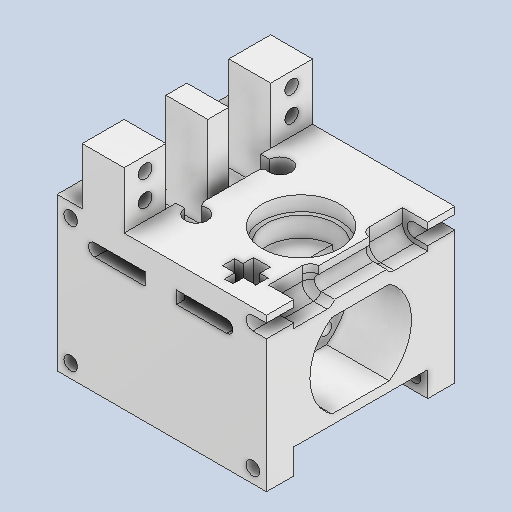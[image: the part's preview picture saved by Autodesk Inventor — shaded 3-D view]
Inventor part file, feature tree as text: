
AUTODESK INVENTOR PART (.ipt)
format: ipt  version: 2024 (Build 280153000, 153)  size: 620,032 bytes
history: native  units: mm
features: extrude x22, sketch x8, other x4, fillet x1
ambient origin geometry x8: Origin, YZ Plane, XZ Plane, XY Plane, X Axis, Y Axis, Z Axis, Center Point
bodies: Body1 (feature_tree)
feature tree (35):
  other  "Bryła1"
  extrude  "Wyciągnięcie proste1"  Depth=90.0mm
  sketch  "Szkic2"
  other  "Płaszczyzna konstrukcyjna1"
  extrude  "Wyciągnięcie proste2"  Depth=100.0mm
  extrude  "Wyciągnięcie proste3"  Depth=73.0mm TaperAngle=0.0deg
  sketch  "Szkic3"
  extrude  "Wyciągnięcie proste4"  Depth=6.5mm
  extrude  "Wyciągnięcie proste5"  Depth=6.5mm
  extrude  "Wyciągnięcie proste6"  Depth=6.5mm
  extrude  "Wyciągnięcie proste7"  Depth=6.5mm
  sketch  "Szkic4"
  extrude  "Wyciągnięcie proste8"  Depth=6.5mm
  extrude  "Wyciągnięcie proste9"  Depth=6.5mm
  extrude  "Wyciągnięcie proste10"  Depth=11.0mm
  extrude  "Wyciągnięcie proste11"  [1 undecoded]
  extrude  "Wyciągnięcie proste12"  Depth=64.0mm TaperAngle=0.0deg
  other  "Płaszczyzna konstrukcyjna2"
  extrude  "Wyciągnięcie proste13"  TaperAngle=0.0deg  [1 undecoded]
  extrude  "Wyciągnięcie proste14"  Depth=36.5mm
  extrude  "Wyciągnięcie proste15"  Depth=45.0mm
  extrude  "Wyciągnięcie proste16"  Depth=28.5mm
  extrude  "Wyciągnięcie proste17"  Depth=48.5mm
  sketch  "Szkic8"
  extrude  "Wyciągnięcie proste18"  Depth=40.0mm
  extrude  "Wyciągnięcie proste19"  Depth=20.0mm
  extrude  "Wyciągnięcie proste20"  Depth=38.0mm
  other  "Płaszczyzna konstrukcyjna3"
  extrude  "Wyciągnięcie proste21"  Depth=5.5mm
  extrude  "Wyciągnięcie proste22"  TaperAngle=45.0deg  [1 undecoded]
  fillet  "Zaokrąglenie1"  [1 undecoded]
  sketch  "Szkic1"
  sketch  "Szkic5"
  sketch  "Szkic6"
  sketch  "Szkic7"
note: 4 required parameter values undecoded (feature->parameter linkage not recoverable at this tier; creation-order binding heuristic only, values carry confidence <= 0.55)
